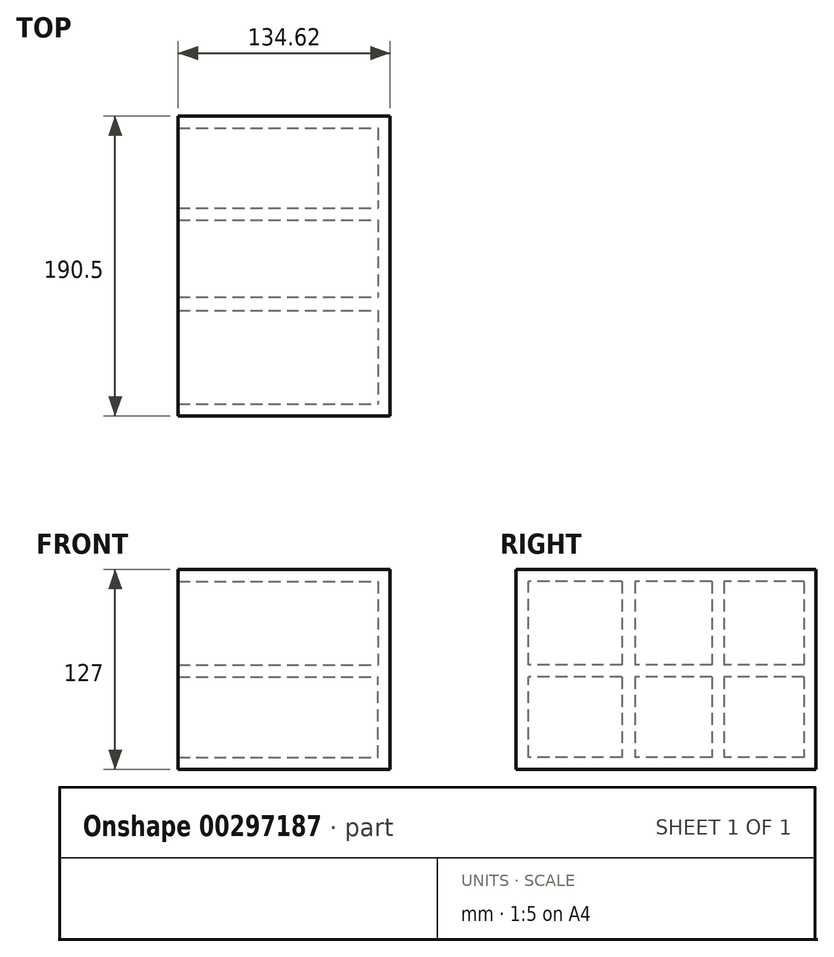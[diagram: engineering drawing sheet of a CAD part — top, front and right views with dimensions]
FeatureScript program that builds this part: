
annotation { "Feature Type Name" : "Feature", "Feature Type Description" : "" }
export const myFeature = defineFeature(function(context is Context, id is Id, definition is map)
    precondition{}
    {
        {
            var Q0;
            Q0=qCreatedBy(makeId("Right.planeOp"),FACE);
            var sketch = newSketch(context, id + "F0", { "sketchPlane" : qUnion([Q0])});
            skLineSegment(sketch, "E0.bottom", {"start": v(-62.58, 64.37) * mm, "end": v(127.92, 64.37) * mm});
            skLineSegment(sketch, "E0.top", {"start": v(-62.58, -62.63) * mm, "end": v(127.92, -62.63) * mm});
            skLineSegment(sketch, "E0.left", {"start": v(-62.58, 64.37) * mm, "end": v(-62.58, -62.63) * mm});
            skLineSegment(sketch, "E0.right", {"start": v(127.92, 64.37) * mm, "end": v(127.92, -62.63) * mm});
            skSolve(sketch);
        }
        {
            var Q0;
            Q0 = qSketchRegion(id + "F0", true);
            extrude(context, id + "F1", {"entities" : qUnion([Q0]), "depth" : 7.62 * mm});
        }
        {
            var Q0;
            Q0=makeQuery(id+"F1.opExtrude","CAP_FACE",FACE,{"disambiguationData":[OSD([sQuery(id+"F0.wireOp",EDGE,"E0.bottom"),sQuery(id+"F0.wireOp",EDGE,"E0.top"),sQuery(id+"F0.wireOp",EDGE,"E0.left"),sQuery(id+"F0.wireOp",EDGE,"E0.right")])],"isStart":true});
            var sketch = newSketch(context, id + "F2", { "sketchPlane" : qUnion([Q0])});
            skLineSegment(sketch, "E1.bottom", {"start": v(-127.92, 64.37) * mm, "end": v(62.58, 64.37) * mm});
            skLineSegment(sketch, "E1.top", {"start": v(-127.92, 56.72) * mm, "end": v(62.58, 56.72) * mm});
            skLineSegment(sketch, "E1.left", {"start": v(-127.92, 64.37) * mm, "end": v(-127.92, 56.72) * mm});
            skLineSegment(sketch, "E1.right", {"start": v(62.58, 64.37) * mm, "end": v(62.58, 56.72) * mm});
            skLineSegment(sketch, "E2.bottom", {"start": v(-127.92, 64.37) * mm, "end": v(-120.2, 64.37) * mm});
            skLineSegment(sketch, "E2.top", {"start": v(-127.92, -62.63) * mm, "end": v(-120.2, -62.63) * mm});
            skLineSegment(sketch, "E2.left", {"start": v(-127.92, 64.37) * mm, "end": v(-127.92, -62.63) * mm});
            skLineSegment(sketch, "E2.right", {"start": v(-120.2, 64.37) * mm, "end": v(-120.2, -62.63) * mm});
            skLineSegment(sketch, "E3.bottom", {"start": v(-127.92, -62.63) * mm, "end": v(62.58, -62.63) * mm});
            skLineSegment(sketch, "E3.top", {"start": v(-127.92, -54.99) * mm, "end": v(62.58, -54.99) * mm});
            skLineSegment(sketch, "E3.left", {"start": v(-127.92, -62.63) * mm, "end": v(-127.92, -54.99) * mm});
            skLineSegment(sketch, "E3.right", {"start": v(62.58, -62.63) * mm, "end": v(62.58, -54.99) * mm});
            skLineSegment(sketch, "E4.bottom", {"start": v(62.58, -62.63) * mm, "end": v(54.87, -62.63) * mm});
            skLineSegment(sketch, "E4.top", {"start": v(62.58, 64.37) * mm, "end": v(54.87, 64.37) * mm});
            skLineSegment(sketch, "E4.left", {"start": v(62.58, -62.63) * mm, "end": v(62.58, 64.37) * mm});
            skLineSegment(sketch, "E4.right", {"start": v(54.87, -62.63) * mm, "end": v(54.87, 64.37) * mm});
            skSolve(sketch);
        }
        {
            var Q0;
            Q0 = qSketchRegion(id + "F2", true);
            extrude(context, id + "F3", {"entities" : qUnion([Q0]), "operationType" : NewBodyOperationType.ADD, "depth" : 127 * mm});
        }
        {
            var Q0;
            Q0=makeQuery(id+"F1.opExtrude","CAP_FACE",FACE,{"disambiguationData":[OSD([sQuery(id+"F0.wireOp",EDGE,"E0.bottom"),sQuery(id+"F0.wireOp",EDGE,"E0.top"),sQuery(id+"F0.wireOp",EDGE,"E0.left"),sQuery(id+"F0.wireOp",EDGE,"E0.right")])],"isStart":true});
            var sketch = newSketch(context, id + "F4", { "sketchPlane" : qUnion([Q0])});
            skLineSegment(sketch, "E5.right", {"start": v(-69.43, 56.72) * mm, "end": v(-69.43, -24.83) * mm});
            skLineSegment(sketch, "E6.bottom", {"start": v(-69.43, 56.72) * mm, "end": v(-61.82, 56.72) * mm});
            skLineSegment(sketch, "E6.top", {"start": v(-69.43, -54.99) * mm, "end": v(-61.82, -54.99) * mm});
            skLineSegment(sketch, "E6.left", {"start": v(-69.43, 56.72) * mm, "end": v(-69.43, -54.99) * mm});
            skLineSegment(sketch, "E6.right", {"start": v(-61.82, 56.72) * mm, "end": v(-61.82, -54.99) * mm});
            skLineSegment(sketch, "E7.right", {"start": v(-4.55, 56.72) * mm, "end": v(-4.55, -8.66) * mm});
            skLineSegment(sketch, "E8.bottom", {"start": v(-4.55, 56.72) * mm, "end": v(-12.88, 56.72) * mm});
            skLineSegment(sketch, "E8.top", {"start": v(-4.55, -54.99) * mm, "end": v(-12.88, -54.99) * mm});
            skLineSegment(sketch, "E8.left", {"start": v(-4.55, 56.72) * mm, "end": v(-4.55, -54.99) * mm});
            skLineSegment(sketch, "E8.right", {"start": v(-12.88, 56.72) * mm, "end": v(-12.88, -54.99) * mm});
            skLineSegment(sketch, "E9.bottom", {"start": v(-120.2, 56.72) * mm, "end": v(-112.2, 56.72) * mm});
            skLineSegment(sketch, "E9.left", {"start": v(-120.2, 56.72) * mm, "end": v(-120.2, 0) * mm});
            skLineSegment(sketch, "E10.top", {"start": v(-120.2, 3.77) * mm, "end": v(-110.68, 3.77) * mm});
            skLineSegment(sketch, "E10.left", {"start": v(-120.2, 0) * mm, "end": v(-120.2, 3.77) * mm});
            skLineSegment(sketch, "E11.left", {"start": v(-120.2, 0) * mm, "end": v(-120.2, -3.84) * mm});
            skLineSegment(sketch, "E12.bottom", {"start": v(-120.2, 3.77) * mm, "end": v(54.87, 3.77) * mm});
            skLineSegment(sketch, "E12.top", {"start": v(-120.2, -3.84) * mm, "end": v(54.87, -3.84) * mm});
            skLineSegment(sketch, "E12.left", {"start": v(-120.2, 3.77) * mm, "end": v(-120.2, -3.84) * mm});
            skLineSegment(sketch, "E12.right", {"start": v(54.87, 3.77) * mm, "end": v(54.87, -3.84) * mm});
            skSolve(sketch);
        }
        {
            var Q0;
            Q0 = qSketchRegion(id + "F4", true);
            extrude(context, id + "F5", {"entities" : qUnion([Q0]), "operationType" : NewBodyOperationType.ADD, "depth" : 127 * mm});
        }
    });
